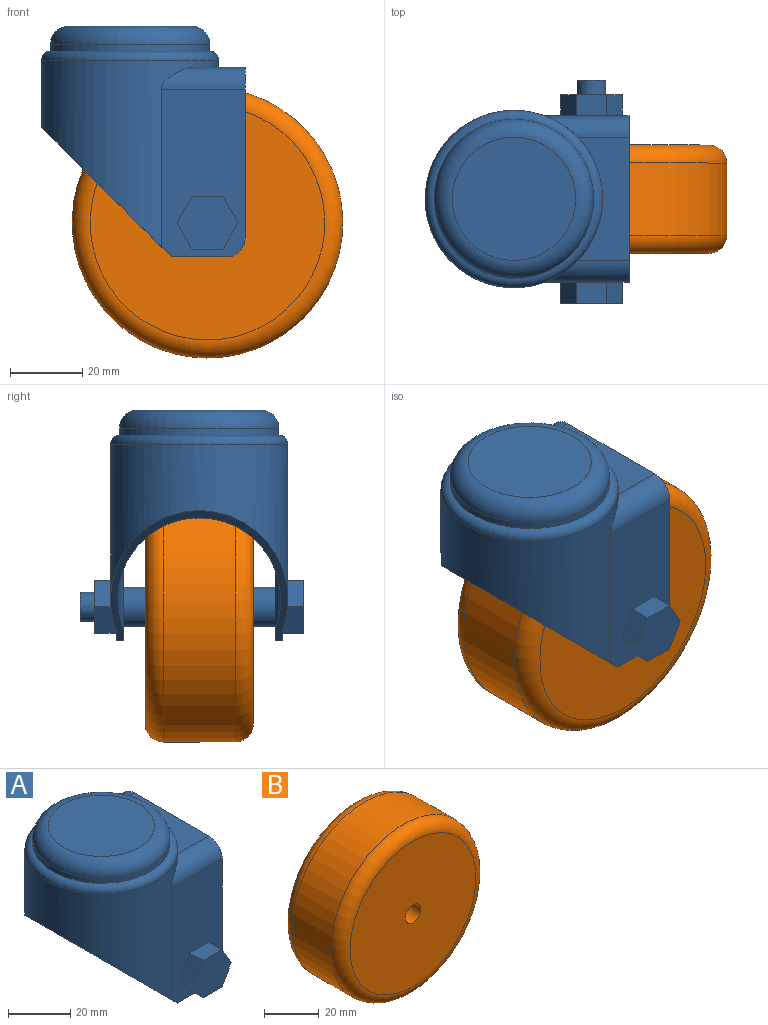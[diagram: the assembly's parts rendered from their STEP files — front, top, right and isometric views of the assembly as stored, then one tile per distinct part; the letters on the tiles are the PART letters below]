
ASSEMBLY  parts=2 mates=1
PART A: 48 faces, bbox 58.5x62x64 mm
  f0: plane 17x14.72mm, normal (0,1,0), area 137.4mm2, adj f34,f42,f43,f44,f45,f46,f47
  f1: plane 17x14.72mm, normal (0,-1,0), area 187.7mm2, adj f36,f37,f38,f39,f40,f41
  f2: plane 46.53x23.59mm, normal (0,-1,0), area 991.9mm2, adj f4,f5,f6,f20,f26,f30,f32
  f3: plane 46.53x23.59mm, normal (0,1,0), area 991.9mm2, adj f5,f6,f7,f18,f26,f28,f31
  f4: plane 15.39x2mm, normal (0,0,-1), area 30.8mm2, adj f2,f6,f21,f32
  f5: cylinder r=22.58mm len=50.56mm, axis (0,0,1), area 2957mm2, adj f2,f3,f6,f14,f18,f19,f20
  f6: plane 49.17x36.08mm, normal (-0.71,0,-0.71), area 275.7mm2, adj f2,f3,f4,f5,f7,f8,f21,f25
  f7: plane 15.39x2mm, normal (0,0,-1), area 30.8mm2, adj f3,f6,f25,f31
  f8: cylinder r=24.58mm len=51.68mm, axis (0,0,1), area 3104.4mm2, adj f6,f15,f21,f22,f23,f24,f25
  f9: plane 34.17x34.17mm, normal (0,0,1), area 916.8mm2, adj f17
  f10: plane 34.17x34.17mm, normal (0,0,-1), area 916.8mm2, adj f11
  f11: torus R=17.08mm, axis (0,0,1), area 562.4mm2, adj f10,f12
  f12: cylinder r=20.08mm len=40.17mm, axis (0,0,1), area 347mm2, adj f11,f13
  f13: torus R=21.33mm, axis (0,0,1), area 253.4mm2, adj f12,f14
  f14: torus R=21.33mm, axis (0,0,1), area 273mm2, adj f5,f13
  f15: torus R=22.08mm, axis (0,0,1), area 584.2mm2, adj f8,f16
  f16: cylinder r=22.08mm len=44.17mm, axis (0,0,1), area 277.5mm2, adj f15,f17
  f17: torus R=17.08mm, axis (0,0,1), area 1000.1mm2, adj f9,f16
  f18: cylinder r=4mm len=23.59mm, axis (1,0,0), area 131mm2, adj f3,f5,f19,f26
  f19: plane 34x17.03mm, normal (0,0,-1), area 396.9mm2, adj f5,f18,f20,f26
  f20: cylinder r=4mm len=23.59mm, axis (1,0,0), area 131mm2, adj f2,f5,f19,f26
  f21: plane 46.53x23.21mm, normal (0,1,0), area 883mm2, adj f4,f6,f8,f22,f26,f32,f42,f43
  f22: cylinder r=6mm len=23.21mm, axis (1,0,0), area 181.7mm2, adj f8,f21,f23,f26
  f23: plane 34x14.13mm, normal (0,0,1), area 321mm2, adj f8,f22,f24,f26
  f24: cylinder r=6mm len=23.21mm, axis (1,0,0), area 181.7mm2, adj f8,f23,f25,f26
  f25: plane 46.53x23.21mm, normal (0,-1,0), area 883mm2, adj f6,f7,f8,f24,f26,f31,f36,f37
  f26: plane 47.53x46mm, normal (1,0,0), area 265.5mm2, adj f2,f3,f18,f19,f20,f21,f22,f23
  f27: plane 11x11mm, normal (0,1,0), area 44.8mm2, adj f28,f33
  f28: cylinder r=5.5mm len=11mm, axis (0,-1,0), area 207.3mm2, adj f3,f27
  f29: plane 11x11mm, normal (0,-1,0), area 44.8mm2, adj f30,f33
  f30: cylinder r=5.5mm len=11mm, axis (0,1,0), area 207.3mm2, adj f2,f29
  f31: cylinder r=5mm len=5mm, axis (0,-1,0), area 15.7mm2, adj f3,f7,f25,f26
  f32: cylinder r=5mm len=5mm, axis (0,-1,0), area 15.7mm2, adj f2,f4,f21,f26
  f33: cylinder r=4mm len=30mm, axis (0,1,0), area 754mm2, adj f27,f29
  f34: cylinder r=4mm len=8mm, axis (0,1,0), area 100.5mm2, adj f0,f35
  f35: plane 8x8mm, normal (0,1,0), area 50.3mm2, adj f34
  f36: plane 8.5x6mm, normal (0,0,1), area 51mm2, adj f1,f25,f39,f41
  f37: plane 7.36x6mm, normal (0.87,0,-0.5), area 51mm2, adj f1,f25,f39,f40
  f38: plane 7.36x6mm, normal (-0.87,0,-0.5), area 51mm2, adj f1,f25,f40,f41
  f39: plane 7.36x6mm, normal (0.87,0,0.5), area 51mm2, adj f1,f25,f36,f37
  f40: plane 8.5x6mm, normal (0,0,-1), area 51mm2, adj f1,f25,f37,f38
  f41: plane 7.36x6mm, normal (-0.87,0,0.5), area 51mm2, adj f1,f25,f36,f38
  f42: plane 8.5x6mm, normal (0,0,1), area 51mm2, adj f0,f21,f45,f47
  f43: plane 7.36x6mm, normal (-0.87,0,-0.5), area 51mm2, adj f0,f21,f45,f46
  f44: plane 7.36x6mm, normal (0.87,0,-0.5), area 51mm2, adj f0,f21,f46,f47
  f45: plane 7.36x6mm, normal (-0.87,0,0.5), area 51mm2, adj f0,f21,f42,f43
  f46: plane 8.5x6mm, normal (0,0,-1), area 51mm2, adj f0,f21,f43,f44
  f47: plane 7.36x6mm, normal (0.87,0,0.5), area 51mm2, adj f0,f21,f42,f44
PART B: 6 faces, bbox 81.2x30x81.2 mm
  f0: cylinder r=4mm len=30mm, axis (0,1,0), area 754mm2, adj f2,f3
  f1: cylinder r=37.5mm len=75mm, axis (0,1,0), area 4712.4mm2, adj f4,f5
  f2: plane 65x65mm, normal (0,-1,0), area 3268mm2, adj f0,f5
  f3: plane 65x65mm, normal (0,1,0), area 3268mm2, adj f0,f4
  f4: torus R=32.5mm, axis (0,-1,0), area 1760.9mm2, adj f1,f3
  f5: torus R=32.5mm, axis (0,-1,0), area 1760.9mm2, adj f1,f2
PLACE A t=(42.37,0,34.54)mm
PLACE B rot(axis=(0,-1,0),27.7deg) t=(19.48,0,18.28)mm
MATE revolute A.f30 <-> B.f0  axis (0,1,0) through (63.87,-15,-19.96)mm
